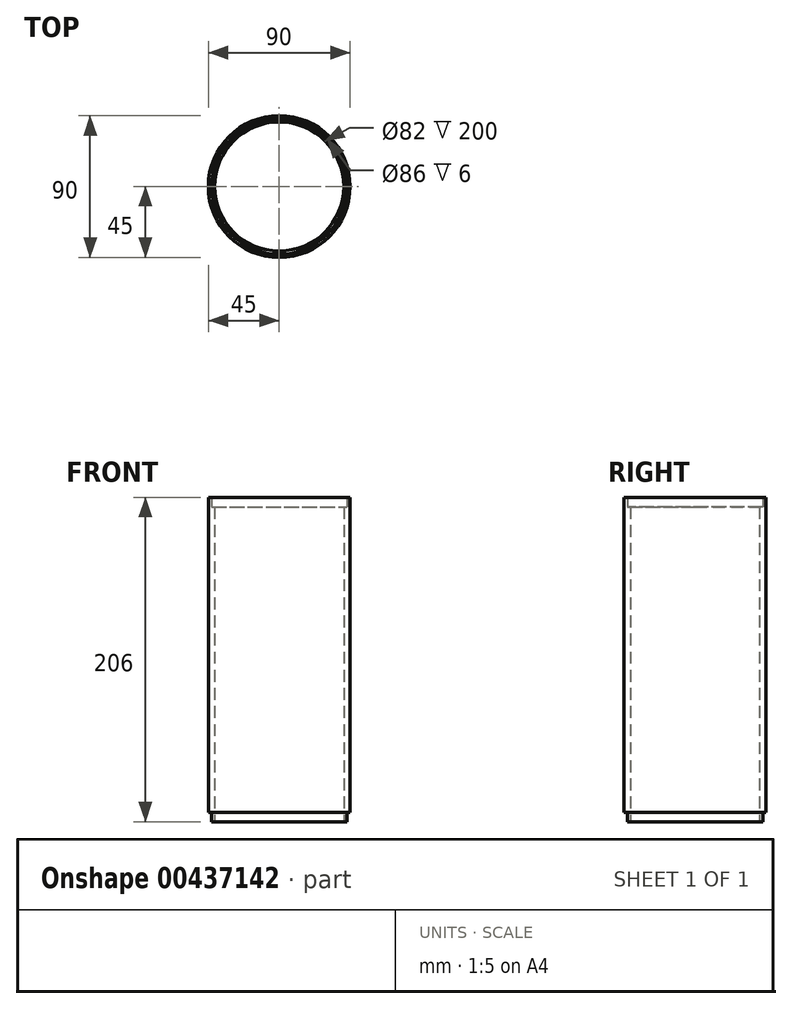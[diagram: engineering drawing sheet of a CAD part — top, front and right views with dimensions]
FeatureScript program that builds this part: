
annotation { "Feature Type Name" : "Feature", "Feature Type Description" : "" }
export const myFeature = defineFeature(function(context is Context, id is Id, definition is map)
    precondition{}
    {
        {
            var Q0;
            Q0=qCreatedBy(makeId("Front.planeOp"),FACE);
            var sketch = newSketch(context, id + "F0", { "sketchPlane" : qUnion([Q0])});
            skLineSegment(sketch, "E0", {"start": v(0, 0) * mm, "end": v(41, 0) * mm, "construction": true});
            skLineSegment(sketch, "E1", {"start": v(41, 0) * mm, "end": v(41, -101.03) * mm});
            skLineSegment(sketch, "E2", {"start": v(41, -101.03) * mm, "end": v(43, -101.03) * mm});
            skLineSegment(sketch, "E3", {"start": v(43, -101.03) * mm, "end": v(43, -95.03) * mm});
            skLineSegment(sketch, "E4", {"start": v(43, -95.03) * mm, "end": v(45, -95.03) * mm});
            skLineSegment(sketch, "E5", {"start": v(45, -95.03) * mm, "end": v(45, 104.97) * mm});
            skLineSegment(sketch, "E6", {"start": v(45, 104.97) * mm, "end": v(43, 104.97) * mm});
            skLineSegment(sketch, "E7", {"start": v(43, 104.97) * mm, "end": v(43, 98.97) * mm});
            skLineSegment(sketch, "E8", {"start": v(43, 98.97) * mm, "end": v(41, 98.97) * mm});
            skLineSegment(sketch, "E9", {"start": v(41, 98.97) * mm, "end": v(41, 0) * mm});
            skLineSegment(sketch, "E10", {"start": v(0, -59.1) * mm, "end": v(0, 57.73) * mm, "construction": true});
            skSolve(sketch);
        }
        {
            var Q0;
            Q0=makeQuery(id+"F0.imprint","IMPRINT",FACE,{"disambiguationData":[TD([[makeQuery(id+"F0.imprint","IMPRINT",EDGE,{"derivedFrom":sQuery(id+"F0.wireOp",EDGE,"E1")}),1.0]])]});
            var Q1;
            Q1=sQuery(id+"F0.wireOp",EDGE,"E10");
            revolve(context, id + "F1", {"entities" : qUnion([Q0]), "axis" : qUnion([Q1]), "revolveType" : RevolveType.FULL});
        }
    });
